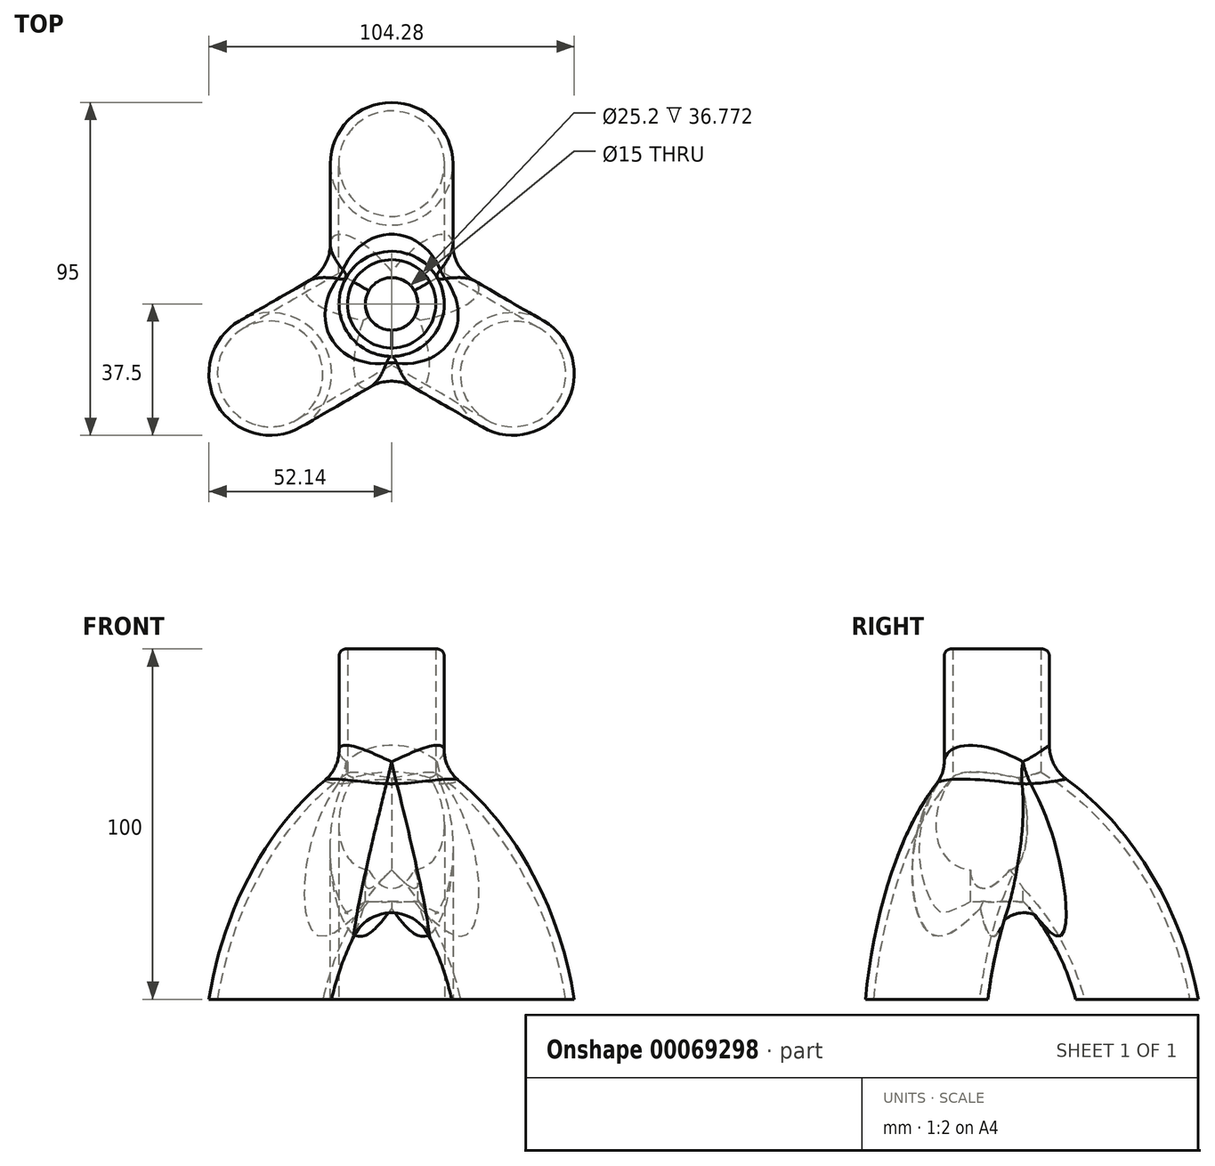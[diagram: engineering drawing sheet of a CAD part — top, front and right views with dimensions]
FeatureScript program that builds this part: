
annotation { "Feature Type Name" : "Feature", "Feature Type Description" : "" }
export const myFeature = defineFeature(function(context is Context, id is Id, definition is map)
    precondition{}
    {
        {
            var Q0;
            Q0=qCreatedBy(makeId("Top.planeOp"),FACE);
            var sketch = newSketch(context, id + "F0", { "sketchPlane" : qUnion([Q0])});
            skCircle(sketch, "E0", {"center": v(0, 0) * mm, "radius": 15 * mm});
            skSolve(sketch);
        }
        {
            var Q0;
            Q0=makeQuery(id+"F0.imprint","IMPRINT",FACE,{"disambiguationData":[TD([[makeQuery(id+"F0.imprint","IMPRINT",EDGE,{"derivedFrom":sQuery(id+"F0.wireOp",EDGE,"E0")}),1.0]])]});
            extrude(context, id + "F1", {"entities" : qUnion([Q0]), "depth" : 50 * mm});
        }
        {
            var Q0;
            Q0=qCreatedBy(makeId("Right.planeOp"),FACE);
            var sketch = newSketch(context, id + "F2", { "sketchPlane" : qUnion([Q0])});
            skFitSpline(sketch, "E1", {"points": [v(40, -50) * mm, v(20, -10.35) * mm, v(0, 5) * mm], "startDerivative": vector(-17.87, 84.4) * mm, "endDerivative": vector(-43.9, 22.45) * mm});
            skSolve(sketch);
        }
        {
            var Q0;
            Q0=makeQuery(id+"F1.opExtrude","CAP_FACE",FACE,{"disambiguationData":[OSD([sQuery(id+"F0.wireOp",EDGE,"E0")])],"isStart":true});
            cPlane(context, id + "F3", {"entities" : qUnion([Q0]), "cplaneType" : CPlaneType.OFFSET, "offset" : 50 * mm, "width" : 150 * mm, "height" : 150 * mm});
        }
        {
            var Q0;
            Q0=qCreatedBy(id+"F3.planeOp",FACE);
            var sketch = newSketch(context, id + "F4", { "sketchPlane" : qUnion([Q0])});
            skCircle(sketch, "E2", {"center": v(0, -40) * mm, "radius": 17.5 * mm});
            skSolve(sketch);
        }
        {
            var Q0;
            Q0=makeQuery(id+"F4.imprint","IMPRINT",FACE,{"disambiguationData":[TD([[makeQuery(id+"F4.imprint","IMPRINT",EDGE,{"derivedFrom":sQuery(id+"F4.wireOp",EDGE,"E2")}),1.0]])]});
            var Q1;
            Q1=sQuery(id+"F2.wireOp",EDGE,"E1");
            sweep(context, id + "F5", {"operationType" : NewBodyOperationType.ADD, "profiles" : qUnion([Q0]), "path" : qUnion([Q1])});
        }
        {
            var Q0;
            Q0=makeQuery(id+"F1.opExtrude","SWEPT_BODY",BODY,{"disambiguationData":[OSD([sQuery(id+"F0.wireOp",EDGE,"E0")])]});
            var Q1;
            Q1=makeQuery(id+"F1.opExtrude","CAP_EDGE",EDGE,{"disambiguationData":[OSD([sQuery(id+"F0.wireOp",EDGE,"E0")])],"isStart":false});
            circularPattern(context, id + "F6", {"entities" : qUnion([Q0]), "axis" : qUnion([Q1]), "angle" : 360 * degree, "instanceCount" : 3, "equalSpace" : true});
        }
        {
            var Q0;
            Q0=makeQuery(id+"F1.opExtrude","SWEPT_BODY",BODY,{"disambiguationData":[OSD([sQuery(id+"F0.wireOp",EDGE,"E0")])]});
            var Q1;
            Q1=makeQuery(id+"F6.opPattern","COPY",BODY,{"derivedFrom":makeQuery(id+"F1.opExtrude","SWEPT_BODY",BODY,{"disambiguationData":[OSD([sQuery(id+"F0.wireOp",EDGE,"E0")])]}),"instanceName":"1"});
            var Q2;
            Q2=makeQuery(id+"F6.opPattern","COPY",BODY,{"derivedFrom":makeQuery(id+"F1.opExtrude","SWEPT_BODY",BODY,{"disambiguationData":[OSD([sQuery(id+"F0.wireOp",EDGE,"E0")])]}),"instanceName":"2"});
            booleanBodies(context, id + "F7", {"operationType" : BooleanOperationType.UNION, "tools" : qUnion([Q0, Q1, Q2])});
        }
        {
            var Q0;
            Q0=makeQuery(id+"F6.opPattern","COPY",FACE,{"derivedFrom":makeQuery(id+"F5.opSweep","CAP_FACE",FACE,{"disambiguationData":[OSD([sQuery(id+"F2.wireOp",VERTEX,"E1.start"),sQuery(id+"F4.wireOp",EDGE,"E2")])],"isStart":true}),"instanceName":"1"});
            var Q1;
            Q1=makeQuery(id+"F5.opSweep","CAP_FACE",FACE,{"disambiguationData":[OSD([sQuery(id+"F2.wireOp",VERTEX,"E1.start"),sQuery(id+"F4.wireOp",EDGE,"E2")])],"isStart":true});
            var Q2;
            Q2=makeQuery(id+"F6.opPattern","COPY",FACE,{"derivedFrom":makeQuery(id+"F5.opSweep","CAP_FACE",FACE,{"disambiguationData":[OSD([sQuery(id+"F2.wireOp",VERTEX,"E1.start"),sQuery(id+"F4.wireOp",EDGE,"E2")])],"isStart":true}),"instanceName":"2"});
            var Q3;
            Q3=makeQuery(id+"F1.opExtrude","CAP_FACE",FACE,{"disambiguationData":[OSD([sQuery(id+"F0.wireOp",EDGE,"E0")])],"isStart":false});
            shell(context, id + "F8", {"entities" : qUnion([Q0, Q1, Q2, Q3]), "thickness" : 2.4 * mm});
        }
        {
            var Q0;
            Q0=makeQuery(id+"F1.opExtrude","CAP_EDGE",EDGE,{"disambiguationData":[OSD([sQuery(id+"F0.wireOp",EDGE,"E0")])],"isStart":false});
            fillet(context, id + "F9", {"entities" : qUnion([Q0]), "radius" : 2 * mm, "tangentPropagation" : true, "allowEdgeOverflow" : false});
        }
        {
            var Q0;
            Q0=qCreatedBy(makeId("Top.planeOp"),FACE);
            var sketch = newSketch(context, id + "F10", { "sketchPlane" : qUnion([Q0])});
            skCircle(sketch, "E3", {"center": v(0, 0) * mm, "radius": 7.5 * mm});
            skSolve(sketch);
        }
        {
            var Q0;
            Q0=makeQuery(id+"F10.imprint","IMPRINT",FACE,{"disambiguationData":[TD([[makeQuery(id+"F10.imprint","IMPRINT",EDGE,{"derivedFrom":sQuery(id+"F10.wireOp",EDGE,"E3")}),1.0]])]});
            extrude(context, id + "F11", {"entities" : qUnion([Q0]), "operationType" : NewBodyOperationType.REMOVE, "oppositeDirection" : true, "depth" : 40.57 * mm});
        }
        {
            var Q0;
            {var subQ0=makeQuery(id+"F1.opExtrude","SWEPT_FACE",FACE,{"disambiguationData":[OSD([sQuery(id+"F0.wireOp",EDGE,"E0")])]});Q0=makeQuery(id+"F7.opBoolean","INTERSECT",EDGE,{"derivedFrom":[subQ0,makeQuery(id+"F6.opPattern","COPY",FACE,{"derivedFrom":subQ0,"instanceName":"2"})]});}
            var Q1;
            Q1=makeQuery(id+"F5.boolean.opBoolean","INTERSECT",EDGE,{"derivedFrom":[makeQuery(id+"F1.opExtrude","SWEPT_FACE",FACE,{"disambiguationData":[OSD([sQuery(id+"F0.wireOp",EDGE,"E0")])]}),makeQuery(id+"F5.opSweep","SWEPT_FACE",FACE,{"disambiguationData":[OSD([sQuery(id+"F2.wireOp",EDGE,"E1"),sQuery(id+"F4.wireOp",EDGE,"E2")])]})]});
            var Q2;
            {var subQ0=makeQuery(id+"F1.opExtrude","SWEPT_FACE",FACE,{"disambiguationData":[OSD([sQuery(id+"F0.wireOp",EDGE,"E0")])]});Q2=makeQuery(id+"F7.opBoolean","INTERSECT",EDGE,{"derivedFrom":[subQ0,makeQuery(id+"F6.opPattern","COPY",FACE,{"derivedFrom":subQ0,"instanceName":"1"})]});}
            var Q3;
            {var subQ0=makeQuery(id+"F5.opSweep","SWEPT_FACE",FACE,{"disambiguationData":[OSD([sQuery(id+"F2.wireOp",EDGE,"E1"),sQuery(id+"F4.wireOp",EDGE,"E2")])]});Q3=makeQuery(id+"F7.opBoolean","INTERSECT",EDGE,{"derivedFrom":[makeQuery(id+"F6.opPattern","COPY",FACE,{"derivedFrom":subQ0,"instanceName":"1"}),makeQuery(id+"F6.opPattern","COPY",FACE,{"derivedFrom":subQ0,"instanceName":"2"})]});}
            var Q4;
            {var subQ0=makeQuery(id+"F5.opSweep","SWEPT_FACE",FACE,{"disambiguationData":[OSD([sQuery(id+"F2.wireOp",EDGE,"E1"),sQuery(id+"F4.wireOp",EDGE,"E2")])]});Q4=makeQuery(id+"F7.opBoolean","INTERSECT",EDGE,{"derivedFrom":[subQ0,makeQuery(id+"F6.opPattern","COPY",FACE,{"derivedFrom":subQ0,"instanceName":"2"})]});}
            var Q5;
            {var subQ0=makeQuery(id+"F5.opSweep","SWEPT_FACE",FACE,{"disambiguationData":[OSD([sQuery(id+"F2.wireOp",EDGE,"E1"),sQuery(id+"F4.wireOp",EDGE,"E2")])]});Q5=makeQuery(id+"F7.opBoolean","INTERSECT",EDGE,{"derivedFrom":[subQ0,makeQuery(id+"F6.opPattern","COPY",FACE,{"derivedFrom":subQ0,"instanceName":"1"})]});}
            fillet(context, id + "F12", {"entities" : qUnion([Q0, Q1, Q2, Q3, Q4, Q5]), "radius" : 12 * mm, "tangentPropagation" : true, "allowEdgeOverflow" : false});
        }
    });
